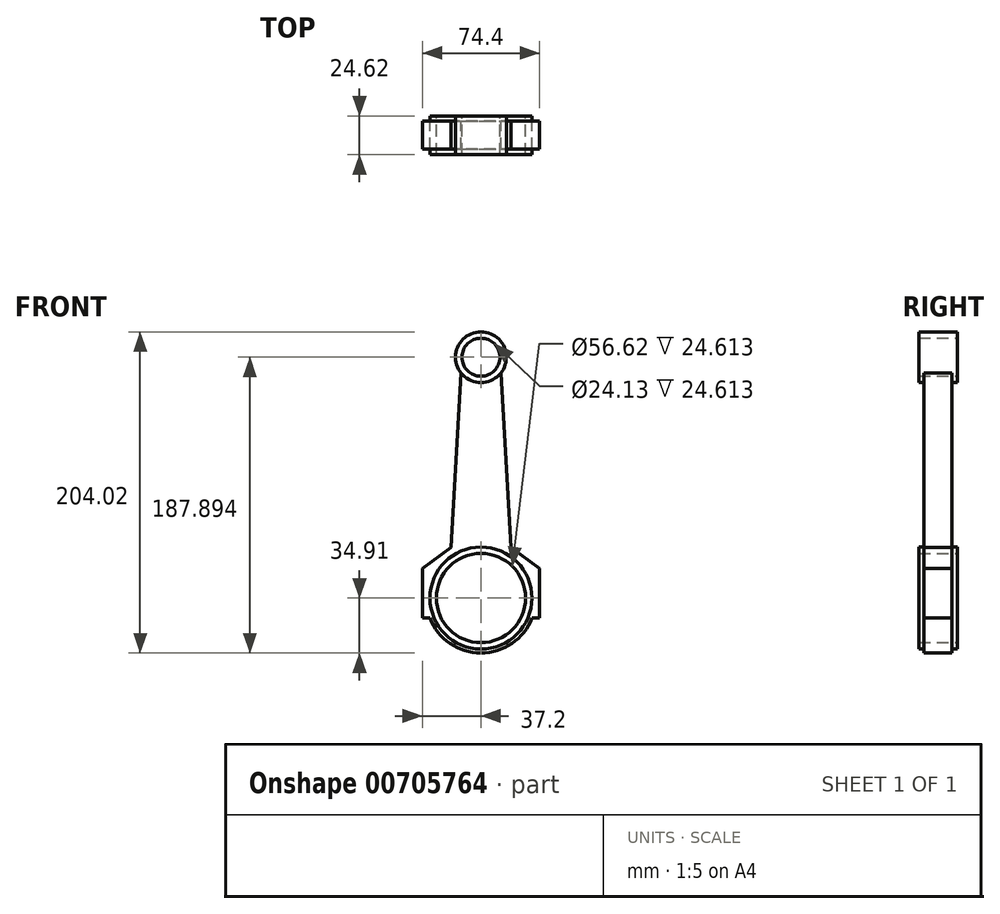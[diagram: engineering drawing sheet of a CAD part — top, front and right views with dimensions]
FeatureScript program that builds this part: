
annotation { "Feature Type Name" : "Feature", "Feature Type Description" : "" }
export const myFeature = defineFeature(function(context is Context, id is Id, definition is map)
    precondition{}
    {
        {
            var Q0;
            Q0=qCreatedBy(makeId("Front.planeOp"),FACE);
            var sketch = newSketch(context, id + "F0", { "sketchPlane" : qUnion([Q0])});
            skCircle(sketch, "E0", {"center": v(0, 0) * mm, "radius": 28.3 * mm});
            skCircle(sketch, "E1", {"center": v(0, 152.98) * mm, "radius": 12.07 * mm});
            skCircle(sketch, "E2.0", {"center": v(0, 152.98) * mm, "radius": 16.13 * mm});
            skCircle(sketch, "E3.0", {"center": v(0, 0) * mm, "radius": 32.37 * mm});
            skLineSegment(sketch, "E4", {"start": v(0, 0) * mm, "end": v(-37.2, 0) * mm});
            skLineSegment(sketch, "E5", {"start": v(-37.2, 0) * mm, "end": v(-37.2, 18.85) * mm});
            skLineSegment(sketch, "E6", {"start": v(-37.2, 18.85) * mm, "end": v(-19.15, 32.2) * mm});
            skLineSegment(sketch, "E7", {"start": v(-19.15, 32.2) * mm, "end": v(-12.65, 142.98) * mm});
            skLineSegment(sketch, "E8", {"start": v(0, 152.98) * mm, "end": v(0, 0) * mm, "construction": true});
            skLineSegment(sketch, "E9.MirrorCS", {"start": v(19.15, 32.2) * mm, "end": v(12.65, 142.98) * mm});
            skLineSegment(sketch, "E10.MirrorCS", {"start": v(37.2, 18.85) * mm, "end": v(19.15, 32.2) * mm});
            skLineSegment(sketch, "E11.MirrorCS", {"start": v(0, 0) * mm, "end": v(37.2, 0) * mm});
            skLineSegment(sketch, "E12.MirrorCS", {"start": v(37.2, 0) * mm, "end": v(37.2, 18.85) * mm});
            skArc(sketch, "E13", {"start": v(-32.52, -12.7) * mm, "mid": v(0, -34.91) * mm, "end": v(32.52, -12.7) * mm});
            skLineSegment(sketch, "E14", {"start": v(-37.2, 0) * mm, "end": v(-37.2, -12.7) * mm});
            skLineSegment(sketch, "E15", {"start": v(-37.2, -12.7) * mm, "end": v(-32.52, -12.7) * mm});
            skLineSegment(sketch, "E16.MirrorCS", {"start": v(37.2, 0) * mm, "end": v(37.2, -12.7) * mm});
            skLineSegment(sketch, "E17.MirrorCS", {"start": v(37.2, -12.7) * mm, "end": v(32.52, -12.7) * mm});
            skPoint(sketch, "E18.orphan", {"position": v(-12.07, 152.98) * mm});
            skPoint(sketch, "E19.orphan", {"position": v(12.06, 152.98) * mm});
            skSolve(sketch);
        }
        {
            var Q0;
            {var subQ0=sQuery(id+"F0.wireOp",EDGE,"E4");var subQ1=sQuery(id+"F0.wireOp",EDGE,"E0");var subQ2=makeQuery(id+"F0.imprint","INTERSECT",VERTEX,{"derivedFrom":[subQ1,subQ0]});Q0=makeQuery(id+"F0.imprint","IMPRINT",FACE,{"disambiguationData":[TD([[makeQuery(id+"F0.imprint","IMPRINT",EDGE,{"disambiguationData":[TD([[subQ2,1.0]])],"derivedFrom":subQ1}),-1.0]])]});}
            extrude(context, id + "F1", {"entities" : qUnion([Q0]), "endBound" : BoundingType.SYMMETRIC, "depth" : 24.6 * mm, "offsetDistance" : 25.4 * mm});
        }
        {
            var Q0;
            {var subQ0=sQuery(id+"F0.wireOp",EDGE,"E5");Q0=makeQuery(id+"F0.imprint","IMPRINT",FACE,{"disambiguationData":[TD([[makeQuery(id+"F0.imprint","IMPRINT",EDGE,{"derivedFrom":subQ0}),-1.0]])]});}
            extrude(context, id + "F2", {"entities" : qUnion([Q0]), "operationType" : NewBodyOperationType.ADD, "endBound" : BoundingType.SYMMETRIC, "depth" : 17.78 * mm, "offsetDistance" : 25.4 * mm});
        }
        {
            var Q0;
            Q0=makeQuery(id+"F0.imprint","IMPRINT",FACE,{"disambiguationData":[TD([[makeQuery(id+"F0.imprint","IMPRINT",EDGE,{"derivedFrom":sQuery(id+"F0.wireOp",EDGE,"E1")}),-1.0]])]});
            extrude(context, id + "F3", {"entities" : qUnion([Q0]), "operationType" : NewBodyOperationType.ADD, "endBound" : BoundingType.SYMMETRIC, "depth" : 24.6 * mm, "offsetDistance" : 25.4 * mm});
        }
        {
            var Q0;
            {var subQ0=sQuery(id+"F0.wireOp",EDGE,"E4");var subQ1=sQuery(id+"F0.wireOp",EDGE,"E0");var subQ2=makeQuery(id+"F0.imprint","INTERSECT",VERTEX,{"derivedFrom":[subQ1,subQ0]});Q0=makeQuery(id+"F0.imprint","IMPRINT",FACE,{"disambiguationData":[TD([[makeQuery(id+"F0.imprint","IMPRINT",EDGE,{"disambiguationData":[TD([[subQ2,-1.0]])],"derivedFrom":subQ1}),-1.0]])]});}
            extrude(context, id + "F4", {"entities" : qUnion([Q0]), "endBound" : BoundingType.SYMMETRIC, "depth" : 24.6 * mm, "offsetDistance" : 25.4 * mm});
        }
        {
            var Q0;
            Q0=makeQuery(id+"F0.imprint","IMPRINT",FACE,{"disambiguationData":[TD([[makeQuery(id+"F0.imprint","IMPRINT",EDGE,{"derivedFrom":sQuery(id+"F0.wireOp",EDGE,"E13")}),1.0]])]});
            extrude(context, id + "F5", {"entities" : qUnion([Q0]), "operationType" : NewBodyOperationType.ADD, "endBound" : BoundingType.SYMMETRIC, "depth" : 17.78 * mm, "offsetDistance" : 25.4 * mm});
        }
    });
